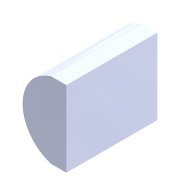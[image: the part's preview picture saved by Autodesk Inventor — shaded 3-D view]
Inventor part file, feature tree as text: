
AUTODESK INVENTOR PART (.ipt)
format: ipt  version: 2022 (Build 260153000, 153)  size: 105,984 bytes
history: native  units: mm
features: plane x2, extrude x1, sketch x1
ambient origin geometry x8: Origin, YZ Plane, XZ Plane, XY Plane, X Axis, Y Axis, Z Axis, Center Point
bodies: Volumenkörper1 (feature_tree)
feature tree (4):
  extrude  "Extrusion1"  Depth=10.0mm
  plane  "Arbeitsebene1"
  plane  "Arbeitsebene2"
  sketch  "Skizze1"  dims[d0=2.0mm d1=10.0mm d2=5.2mm d3=12.0mm d4=0.0mm]
